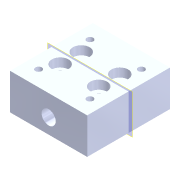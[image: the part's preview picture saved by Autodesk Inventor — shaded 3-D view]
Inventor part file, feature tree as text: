
AUTODESK INVENTOR PART (.ipt)
format: ipt  version: 2022 (Build 260153000, 153)  size: 156,672 bytes
history: mixed  units: mm
features: plane x1, hole x1, imported_body x1
ambient origin geometry x8: Origin, YZ Plane, XZ Plane, XY Plane, X Axis, Y Axis, Z Axis, Center Point
bodies: Volumenkörper1 (imported_parasolid)
feature tree (3):
  plane  "Arbeitsebene1"
  hole  "Hole2"  [1 undecoded]
  imported_body  NMx_Import_Brep_tag  [imported B-rep: ~35 faces, bbox_mm=[30.0, 14.0, 32.2]]
note: 1 required parameter value undecoded (feature->parameter linkage not recoverable at this tier; creation-order binding heuristic only, values carry confidence <= 0.55)
